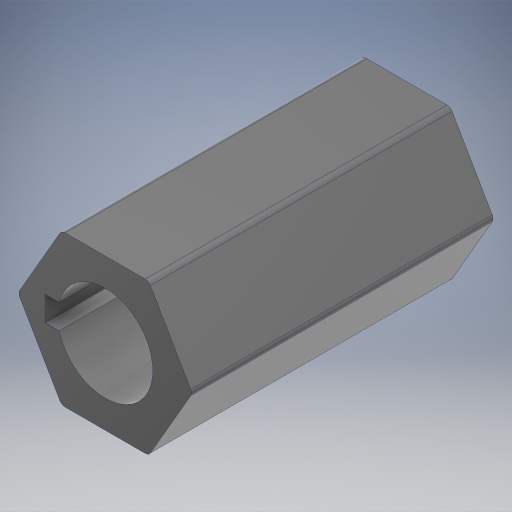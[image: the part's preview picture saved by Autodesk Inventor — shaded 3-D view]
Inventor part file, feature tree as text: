
AUTODESK INVENTOR PART (.ipt)
format: ipt  version: 2024.2 (Build 282272000, 272)  size: 262,144 bytes
history: native  units: in
note: dims shown in document units (in); Inventor stores cm internally (conversion verified against a paired STEP export)
features: fillet x1
ambient origin geometry x8: Origin, YZ Plane, XZ Plane, XY Plane, X Axis, Y Axis, Z Axis, Center Point
bodies: Solid1 (feature_tree)
feature tree (1):
  fillet  "Fillet1"  [1 undecoded]
note: 1 required parameter value undecoded (feature->parameter linkage not recoverable at this tier; creation-order binding heuristic only, values carry confidence <= 0.55)
